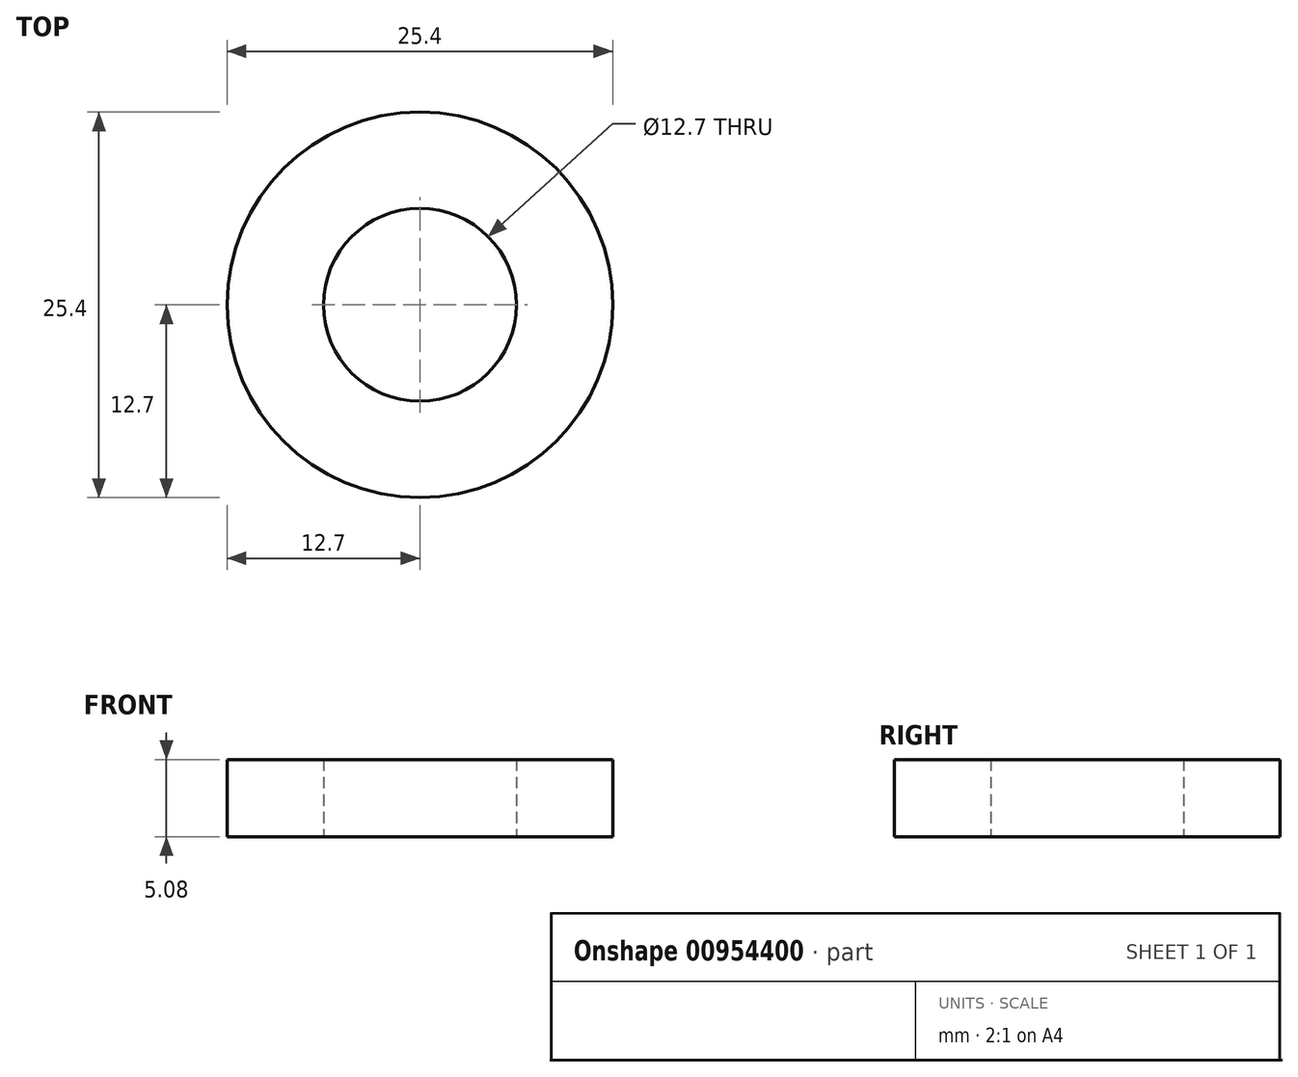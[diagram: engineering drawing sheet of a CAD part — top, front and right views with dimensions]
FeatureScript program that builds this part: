
annotation { "Feature Type Name" : "Feature", "Feature Type Description" : "" }
export const myFeature = defineFeature(function(context is Context, id is Id, definition is map)
    precondition{}
    {
        {
            var Q0;
            Q0=qCreatedBy(makeId("Top.planeOp"),FACE);
            var sketch = newSketch(context, id + "F0", { "sketchPlane" : qUnion([Q0])});
            skCircle(sketch, "E0", {"center": v(0, 0) * mm, "radius": 6.35 * mm});
            skCircle(sketch, "E1", {"center": v(0, 0) * mm, "radius": 12.7 * mm});
            skSolve(sketch);
        }
        {
            var Q0;
            Q0=makeQuery(id+"F0.imprint","IMPRINT",FACE,{"disambiguationData":[TD([[makeQuery(id+"F0.imprint","IMPRINT",EDGE,{"derivedFrom":sQuery(id+"F0.wireOp",EDGE,"E0")}),-1.0]])]});
            extrude(context, id + "F1", {"entities" : qUnion([Q0]), "depth" : 5.08 * mm, "offsetDistance" : 25.4 * mm});
        }
    });
